# Revit family: QF_Hallde_RG400i_test
name_source: partatom
category: Specialty Equipment
revit_build: Autodesk Revit MEP 2012 (Build: 20110916_2132(x64)
units: mm (PartAtom-declared; Revit-internal decimal feet)

## types (1)
- RG-400i
    Apparent Power = 1500 VA
    Assembly Code = E1090320
    Conn Conduit = Yes
    Depth = 590 mm  [stored 1.9357 ft]
    Description = VEGETABLE PREPARATION MACHINE UP TO 2,4 TONS/HOUR WITH MANUAL PUSH FEEDER
    Elec Conn Connection Height = 673 mm  [stored 2.20801 ft]
    FL Amps = 0 A
    Height = 1350 mm  [stored 4.42913 ft]
    Manufacturer = HALLDE
    Max Overcurrent Protection = 10 A
    Min Ckt Ampacity = 0 A
    Model = RG-400i
    Phase = 3
    URL = www.hallde.com
    Watts = 1500 W
    Weight in Pounds = 155
    Width = 490 mm

note: [stored X ft] marks values corroborated as IEEE doubles in the binary element streams (Revit-internal decimal feet)

## geometry (parser evidence)
native form markers: Blend x6, Sweep x2
no freeform markers — native parametric forms only
